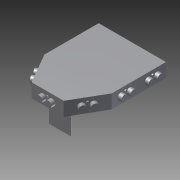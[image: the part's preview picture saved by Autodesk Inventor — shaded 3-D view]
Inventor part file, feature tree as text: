
AUTODESK INVENTOR PART (.ipt)
format: ipt  version: 2012 (Build 160160000, 160)  size: 337,408 bytes
history: native  units: mm
features: extrude x14, sketch x10, hole x1
ambient origin geometry x8: Origin, YZ Plane, XZ Plane, XY Plane, X Axis, Y Axis, Z Axis, Center Point
bodies: Solid1 (feature_tree)
feature tree (25):
  extrude  "Extrusion1"  TaperAngle=150.0deg  [1 undecoded]
  sketch  "Sketch2"  dims[d6=91.026319mm d7=91.026319mm]
  extrude  "Extrusion2"  Depth=91.026319mm
  extrude  "Extrusion3"  Depth=140.933826mm
  sketch  "Sketch3"  dims[d8=83.483681mm d9=140.933826mm]
  extrude  "Extrusion4"  Depth=36.0mm TaperAngle=0.0deg
  extrude  "Extrusion5"  Depth=10.0mm TaperAngle=0.0deg
  sketch  "Sketch4"  dims[d10=140.933826mm d11=36.0mm d12=0.0mm]
  extrude  "Extrusion6"  Depth=3.0mm TaperAngle=0.0deg
  extrude  "Extrusion7"  Depth=10.0mm TaperAngle=0.0deg
  sketch  "Sketch5"  dims[d13=16.5mm d14=16.5mm d15=5.9mm d16=3.0mm d17=7.8mm d18=7.8mm d19=23.4mm d20=7.675mm d21=7.675mm d22=7.675mm d23=7.675mm d24=7.8mm d25=7.8mm d27=6.9mm d29=10.0mm d30=0.0mm]
  extrude  "Extrusion8"  Depth=70.466913mm
  extrude  "Extrusion9"  Depth=35.2335mm
  sketch  "Sketch6"  dims[d31=3.0mm d32=0.0mm]
  extrude  "Extrusion10"  Depth=3.0mm TaperAngle=0.0deg
  extrude  "Extrusion11"  Depth=10.0mm TaperAngle=0.0deg
  sketch  "Sketch7"  dims[d49=16.5mm d50=16.5mm d51=5.9mm d52=3.0mm d53=7.675mm d54=7.675mm d55=23.4mm d56=7.8mm d57=7.8mm d58=7.8mm d59=7.8mm d60=7.675mm d61=7.675mm d62=11.7mm d63=3.0mm d64=0.0mm]
  sketch  "Sketch8"  dims[d65=10.0mm d66=0.0mm]
  extrude  "Extrusion12"  Depth=87.255mm
  extrude  "Extrusion13"  Depth=43.6275mm
  extrude  "Extrusion14"  Depth=10.0mm TaperAngle=0.0deg
  hole  "Hole1"  [1 undecoded]
  sketch  "Sketch1"  dims[d0=120.0deg d1=219.764931mm d2=174.51mm d3=120.0deg d4=150.0deg d5=150.0deg]
  sketch  "Sketch9"  dims[d67=16.5mm d68=16.5mm d69=5.9mm d70=3.0mm d71=-7.675mm d72=7.675mm d73=23.4mm d74=7.8mm d75=7.8mm d76=7.8mm d77=7.8mm d78=7.675mm d79=7.675mm d80=6.9mm d81=11.7mm d82=6.9mm d83=10.0mm d84=0.0mm]
  sketch  "Sketch10"  dims[d85=3.0mm d86=0.0mm d87=16.5mm d88=16.5mm d89=5.9mm d90=3.0mm d91=7.675mm d92=7.675mm d93=23.4mm d94=7.8mm d95=7.8mm d96=7.8mm d97=7.8mm d98=7.675mm d99=7.675mm d100=6.9mm d101=11.7mm d102=6.9mm d103=70.466913mm d104=35.2335mm d105=3.0mm d106=0.0mm d107=10.0mm d108=0.0mm d125=87.255mm d126=43.6275mm d127=16.5mm d128=16.5mm d129=5.9mm d130=3.0mm d131=-7.8mm d132=7.8mm d133=23.4mm d134=7.675mm d135=7.675mm d136=7.675mm d137=7.675mm d138=7.8mm d139=7.8mm d140=11.7mm d141=6.9mm d142=11.7mm d143=10.0mm d144=0.0mm d145=3.0mm d146=0.0mm d147=16.5mm d148=16.5mm d149=5.9mm d150=3.0mm d151=-7.675mm d152=7.675mm d153=23.4mm d154=7.8mm d155=7.8mm d156=7.8mm d157=7.8mm d158=7.675mm d159=7.675mm d160=6.9mm d161=11.7mm d162=6.9mm d165=3.0mm d166=0.0mm d167=10.0mm d168=0.0mm d201=3.0mm d202=3.0mm d203=3.0mm d204=3.0mm d205=3.0mm d206=-5.117mm d207=10.0mm d208=15.117mm d209=10.0mm d210=5.554212mm d211=5.0mm d212=5.0mm d213=5.554212mm d214=5.554212mm d215=5.0mm d216=5.0mm d217=3.0mm d218=3.0mm d219=3.0mm d220=5.117mm d221=0.0mm d222=15.117007mm d223=3.0mm d224=5.0mm d225=5.0mm d226=5.0mm d227=5.000007mm d228=5.0mm d251=28.5mm d252=28.5mm d253=2.0mm d254=67.0mm d255=0.0mm d256=3.0mm d257=3.0mm d258=3.0mm d259=3.0mm d260=3.0mm d261=-5.117mm d262=10.0mm d263=15.117mm d264=10.0mm d265=5.554212mm d266=5.0mm d267=5.0mm d268=5.554212mm d269=5.554212mm d270=5.0mm d271=5.0mm d272=3.0mm d273=3.0mm d274=3.0mm d275=5.117mm d276=0.0mm d277=15.117007mm d278=3.0mm d279=5.0mm d280=5.0mm d281=5.0mm d282=5.000007mm d283=5.0mm d284=28.5mm d285=28.5mm d286=2.0mm d287=3.0mm d288=6.0mm d289=4.0mm d290=2.0mm d291=90.0deg d292=10.0mm d293=20.594885mm]
note: 2 required parameter values undecoded (feature->parameter linkage not recoverable at this tier; creation-order binding heuristic only, values carry confidence <= 0.55)
